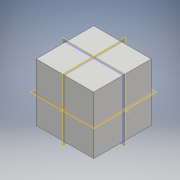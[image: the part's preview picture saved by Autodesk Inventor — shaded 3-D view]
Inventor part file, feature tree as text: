
AUTODESK INVENTOR PART (.ipt)
format: ipt  version: 2017 (Build 210142000, 142)  size: 95,744 bytes
history: native  units: mm
features: plane x3, other x3, extrude x1, sketch x1
ambient origin geometry x8: Origin, YZ Plane, XZ Plane, XY Plane, X Axis, Y Axis, Z Axis, Center Point
bodies: Solid1 (feature_tree)
feature tree (8):
  extrude  "Extrusion1"  Depth=55.88mm
  plane  "Work Plane1"
  plane  "Work Plane2"
  plane  "Work Plane3"
  other  "Work Axis1"
  other  "Work Axis2"
  other  "Work Axis3"
  sketch  "Sketch1"  dims[d0=55.88mm d1=55.88mm d2=55.88mm d3=0.0mm]
